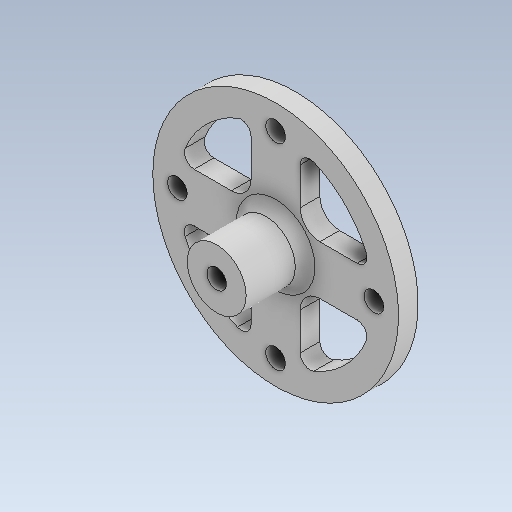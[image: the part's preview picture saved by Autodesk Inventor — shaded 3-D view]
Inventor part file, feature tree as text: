
AUTODESK INVENTOR PART (.ipt)
format: ipt  version: 2023 (Build 270158000, 158)  size: 250,368 bytes
history: native  units: mm
features: sketch x5, extrude x4, other x4, fillet x3, projected_geometry x2, hole x1, pattern_circular x1, reference x1
ambient origin geometry x8: Origin, YZ Plane, XZ Plane, XY Plane, X Axis, Y Axis, Z Axis, Center Point
bodies: Solid1 (feature_tree)
feature tree (21):
  extrude  "Extrusion1"  Depth=5.0mm
  hole  "Hole1"  [1 undecoded]
  extrude  "Extrusion2"  Depth=2.0mm
  fillet  "Fillet1"  Radius=1.0mm
  fillet  "Fillet2"  Radius=2.0mm
  extrude  "Extrusion3"  Depth=1.0mm
  extrude  "Extrusion4"  Depth=1.0mm
  pattern_circular  "Circular Pattern1"  [2 undecoded]
  fillet  "Fillet3"  Radius=40.0mm
  sketch  "Sketch1"  dims[d0=5.0mm d1=5.0mm]
  reference  "Reference1"
  sketch  "Sketch2"  dims[d2=2.0mm d3=0.0mm]
  projected_geometry  "Projected Loop1"
  sketch  "Sketch3"  dims[d4=2.0mm d5=6.0mm d6=4.0mm d7=2.0mm d8=90.0deg d9=5.0mm d10=0.0mm d11=6.0mm]
  sketch  "Sketch4"  dims[d12=6.0mm d13=0.0mm d14=2.0mm d15=1.0mm d16=2.0mm]
  sketch  "Sketch5"  dims[d17=12.0mm d18=0.0mm d19=25.0mm d20=20.0mm d21=2.0mm d22=0.0mm d23=40.0mm d24=360.0deg d26=1.0mm]
  projected_geometry  "Projected Loop2"
  parser-record x1  (decoder bookkeeping rows leaked as tree rows — omitted from the tree; the rows remain in map.json)
  other  "reducer_1.iam"
  other  "mot_27_ass:1"
  other  "mot_27_1:1"
note: 3 required parameter values undecoded (feature->parameter linkage not recoverable at this tier; creation-order binding heuristic only, values carry confidence <= 0.55)
note: 1 file-system path scrubbed to <path> (originals preserved in map.json)
